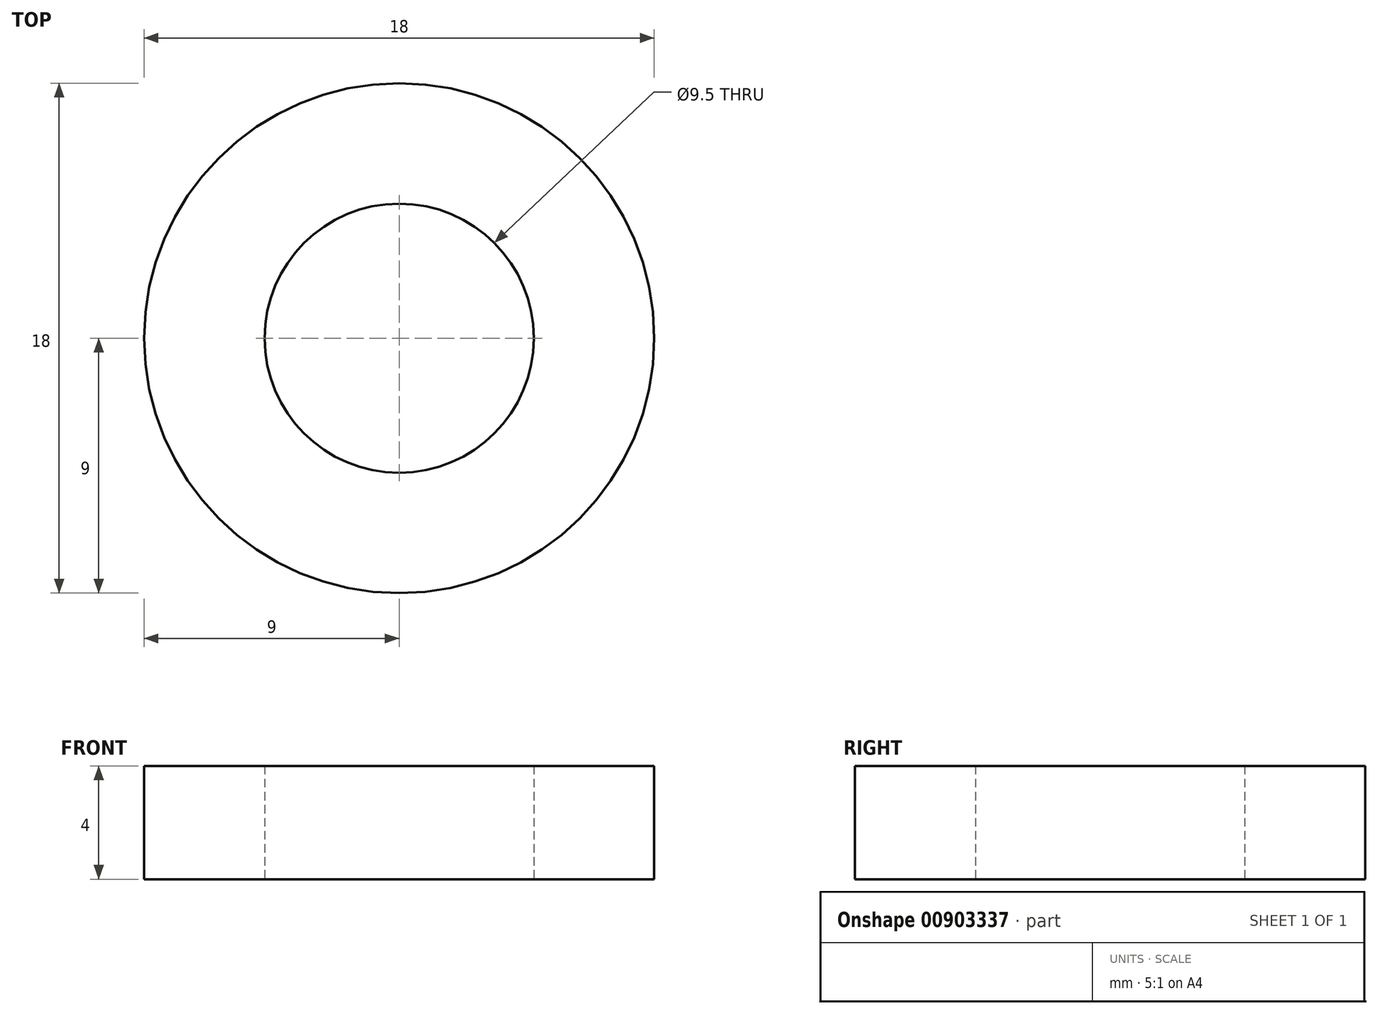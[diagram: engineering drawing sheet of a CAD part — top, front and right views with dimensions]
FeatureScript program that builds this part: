
annotation { "Feature Type Name" : "Feature", "Feature Type Description" : "" }
export const myFeature = defineFeature(function(context is Context, id is Id, definition is map)
    precondition{}
    {
        {
            var Q0;
            Q0=qCreatedBy(makeId("Top.planeOp"),FACE);
            var sketch = newSketch(context, id + "F0", { "sketchPlane" : qUnion([Q0])});
            skCircle(sketch, "E0", {"center": v(0, 0) * mm, "radius": 9 * mm});
            skCircle(sketch, "E1", {"center": v(0, 0) * mm, "radius": 4.75 * mm});
            skSolve(sketch);
        }
        {
            var Q0;
            Q0=makeQuery(id+"F0.imprint","IMPRINT",FACE,{"disambiguationData":[TD([[makeQuery(id+"F0.imprint","IMPRINT",EDGE,{"derivedFrom":sQuery(id+"F0.wireOp",EDGE,"E0")}),1.0]])]});
            extrude(context, id + "F1", {"entities" : qUnion([Q0]), "depth" : 4 * mm, "offsetDistance" : 25 * mm});
        }
    });
